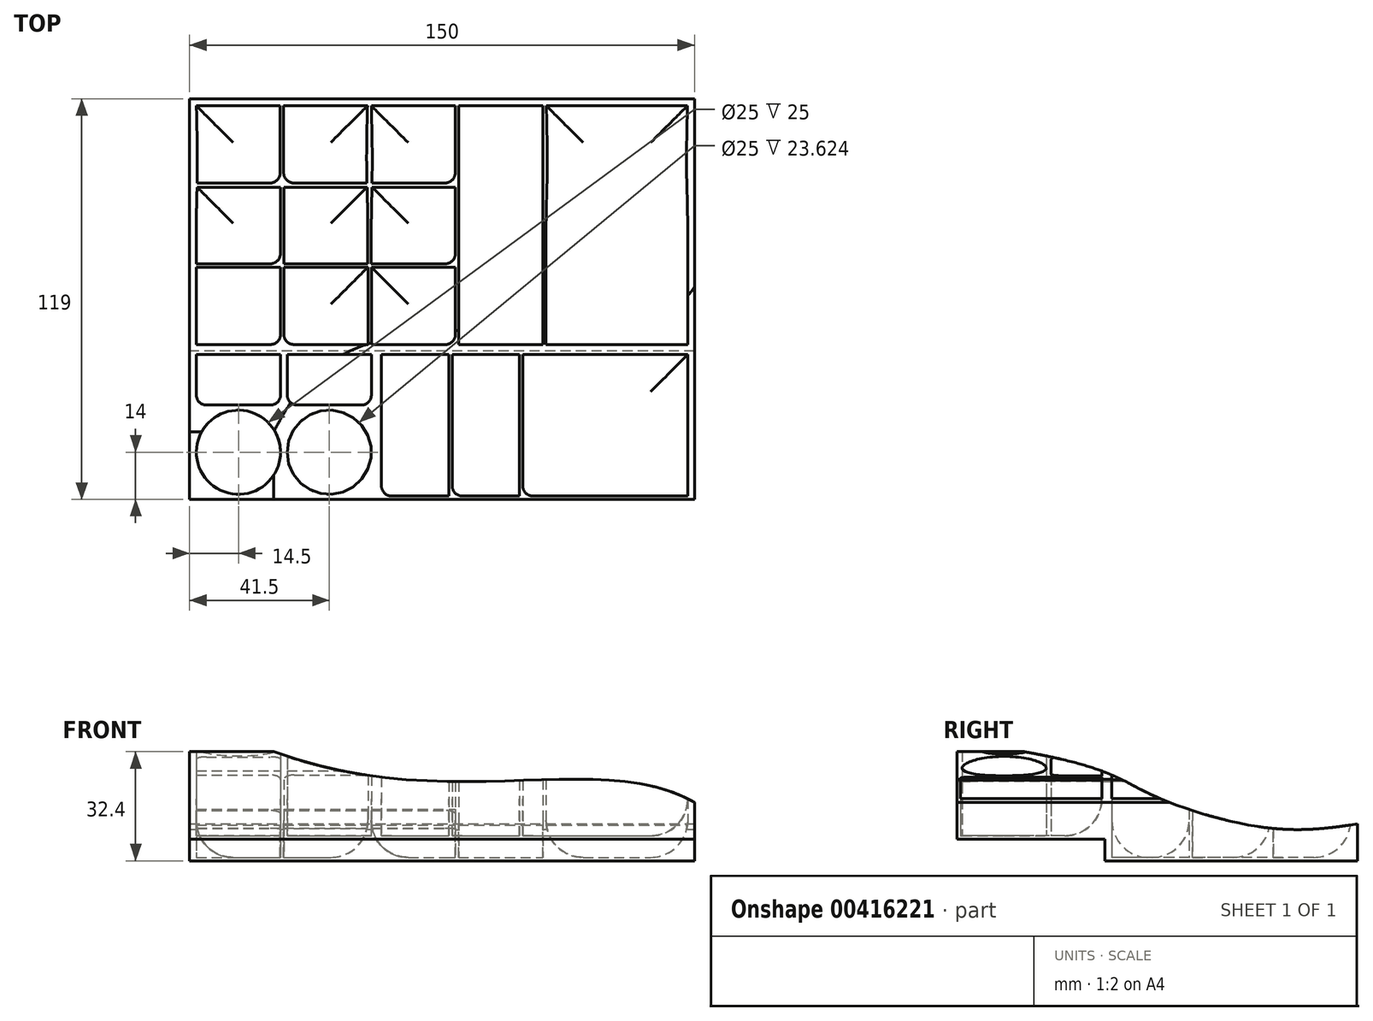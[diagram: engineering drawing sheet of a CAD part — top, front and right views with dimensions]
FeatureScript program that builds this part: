
annotation { "Feature Type Name" : "Feature", "Feature Type Description" : "" }
export const myFeature = defineFeature(function(context is Context, id is Id, definition is map)
    precondition{}
    {
        {
            var Q0;
            Q0=qCreatedBy(makeId("Right.planeOp"),FACE);
            var sketch = newSketch(context, id + "F0", { "sketchPlane" : qUnion([Q0])});
            skLineSegment(sketch, "E0", {"start": v(0, 0) * mm, "end": v(75, 0) * mm});
            skLineSegment(sketch, "E1", {"start": v(0, 0) * mm, "end": v(0, 6.4) * mm});
            skLineSegment(sketch, "E2", {"start": v(0, 6.4) * mm, "end": v(-44, 6.4) * mm});
            skLineSegment(sketch, "E3.0", {"start": v(1, 7.4) * mm, "end": v(-44, 7.4) * mm});
            skLineSegment(sketch, "E3.1", {"start": v(1, 1) * mm, "end": v(1, 7.4) * mm});
            skLineSegment(sketch, "E3.2", {"start": v(1, 1) * mm, "end": v(75, 1) * mm});
            skLineSegment(sketch, "E4", {"start": v(75, 1) * mm, "end": v(75, 0) * mm});
            skLineSegment(sketch, "E5", {"start": v(-44, 7.4) * mm, "end": v(-44, 6.4) * mm});
            skSolve(sketch);
        }
        {
            var Q0;
            Q0=makeQuery(id+"F0.imprint","IMPRINT",FACE,{"disambiguationData":[TD([[makeQuery(id+"F0.imprint","IMPRINT",EDGE,{"derivedFrom":sQuery(id+"F0.wireOp",EDGE,"E0")}),1.0]])]});
            extrude(context, id + "F1", {"entities" : qUnion([Q0]), "depth" : 150 * mm});
        }
        {
            var Q0;
            Q0=makeQuery(id+"F1.opExtrude","SWEPT_FACE",FACE,{"disambiguationData":[OSD([sQuery(id+"F0.wireOp",EDGE,"E3.0")])]});
            var sketch = newSketch(context, id + "F2", { "sketchPlane" : qUnion([Q0])});
            skCircle(sketch, "E6", {"center": v(14.5, -30) * mm, "radius": 12.5 * mm});
            skCircle(sketch, "E7", {"center": v(41.5, -30) * mm, "radius": 12.5 * mm});
            skLineSegment(sketch, "E8.bottom", {"start": v(2, -1) * mm, "end": v(27, -1) * mm});
            skLineSegment(sketch, "E8.top", {"start": v(2, -16) * mm, "end": v(27, -16) * mm});
            skLineSegment(sketch, "E8.left", {"start": v(2, -1) * mm, "end": v(2, -16) * mm});
            skLineSegment(sketch, "E8.right", {"start": v(27, -1) * mm, "end": v(27, -16) * mm});
            skLineSegment(sketch, "E9.bottom", {"start": v(29, -1) * mm, "end": v(54, -1) * mm});
            skLineSegment(sketch, "E9.top", {"start": v(29, -16) * mm, "end": v(54, -16) * mm});
            skLineSegment(sketch, "E9.left", {"start": v(29, -1) * mm, "end": v(29, -16) * mm});
            skLineSegment(sketch, "E9.right", {"start": v(54, -1) * mm, "end": v(54, -16) * mm});
            skLineSegment(sketch, "E10.bottom", {"start": v(57, -1) * mm, "end": v(77, -1) * mm});
            skLineSegment(sketch, "E10.top", {"start": v(57, -43) * mm, "end": v(77, -43) * mm});
            skLineSegment(sketch, "E10.left", {"start": v(57, -1) * mm, "end": v(57, -43) * mm});
            skLineSegment(sketch, "E10.right", {"start": v(77, -1) * mm, "end": v(77, -43) * mm});
            skLineSegment(sketch, "E11.bottom", {"start": v(78, -1) * mm, "end": v(98, -1) * mm});
            skLineSegment(sketch, "E11.top", {"start": v(78, -43) * mm, "end": v(98, -43) * mm});
            skLineSegment(sketch, "E11.left", {"start": v(78, -1) * mm, "end": v(78, -43) * mm});
            skLineSegment(sketch, "E11.right", {"start": v(98, -1) * mm, "end": v(98, -43) * mm});
            skLineSegment(sketch, "E12.bottom", {"start": v(99, -1) * mm, "end": v(148, -1) * mm});
            skLineSegment(sketch, "E12.top", {"start": v(99, -43) * mm, "end": v(148, -43) * mm});
            skLineSegment(sketch, "E12.left", {"start": v(99, -1) * mm, "end": v(99, -43) * mm});
            skLineSegment(sketch, "E12.right", {"start": v(148, -1) * mm, "end": v(148, -43) * mm});
            skLineSegment(sketch, "E13", {"start": v(27, -1) * mm, "end": v(29, -1) * mm, "construction": true});
            skLineSegment(sketch, "E14", {"start": v(54, -1) * mm, "end": v(57, -1) * mm, "construction": true});
            skLineSegment(sketch, "E15", {"start": v(77, -1) * mm, "end": v(78, -1) * mm, "construction": true});
            skLineSegment(sketch, "E16", {"start": v(98, -1) * mm, "end": v(99, -1) * mm, "construction": true});
            skLineSegment(sketch, "E17", {"start": v(14.5, -30) * mm, "end": v(14.5, -16) * mm, "construction": true});
            skLineSegment(sketch, "E18", {"start": v(41.5, -30) * mm, "end": v(41.5, -16) * mm, "construction": true});
            skLineSegment(sketch, "E19", {"start": v(0, 1) * mm, "end": v(150, 1) * mm});
            skLineSegment(sketch, "E20", {"start": v(150, 1) * mm, "end": v(150, -44) * mm});
            skLineSegment(sketch, "E21", {"start": v(150, -44) * mm, "end": v(0, -44) * mm});
            skLineSegment(sketch, "E22", {"start": v(0, -44) * mm, "end": v(0, 1) * mm});
            skSolve(sketch);
        }
        {
            var Q0;
            Q0=makeQuery(id+"F2.imprint","IMPRINT",FACE,{"disambiguationData":[TD([[makeQuery(id+"F2.imprint","IMPRINT",EDGE,{"derivedFrom":sQuery(id+"F2.wireOp",EDGE,"E6")}),-1.0]])]});
            extrude(context, id + "F3", {"entities" : qUnion([Q0]), "operationType" : NewBodyOperationType.ADD, "depth" : 25 * mm});
        }
        {
            var Q0;
            Q0=makeQuery(id+"F1.opExtrude","SWEPT_FACE",FACE,{"disambiguationData":[OSD([sQuery(id+"F0.wireOp",EDGE,"E3.2")])]});
            var sketch = newSketch(context, id + "F4", { "sketchPlane" : qUnion([Q0])});
            skLineSegment(sketch, "E23.bottom", {"start": v(1.93, 73) * mm, "end": v(26.93, 73) * mm});
            skLineSegment(sketch, "E23.top", {"start": v(1.93, 50) * mm, "end": v(26.93, 50) * mm});
            skLineSegment(sketch, "E23.left", {"start": v(1.93, 73) * mm, "end": v(1.93, 50) * mm});
            skLineSegment(sketch, "E23.right", {"start": v(26.93, 73) * mm, "end": v(26.93, 50) * mm});
            skLineSegment(sketch, "E24.0.1.0", {"start": v(26.96, 49) * mm, "end": v(26.96, 26) * mm});
            skLineSegment(sketch, "E24.0.1.1", {"start": v(1.96, 49) * mm, "end": v(26.96, 49) * mm});
            skLineSegment(sketch, "E24.0.1.2", {"start": v(1.96, 26) * mm, "end": v(26.96, 26) * mm});
            skLineSegment(sketch, "E24.0.1.3", {"start": v(1.96, 49) * mm, "end": v(1.96, 26) * mm});
            skLineSegment(sketch, "E24.0.2.0", {"start": v(27, 25) * mm, "end": v(27, 2) * mm});
            skLineSegment(sketch, "E24.0.2.1", {"start": v(2, 25) * mm, "end": v(27, 25) * mm});
            skLineSegment(sketch, "E24.0.2.2", {"start": v(2, 2) * mm, "end": v(27, 2) * mm});
            skLineSegment(sketch, "E24.0.2.3", {"start": v(2, 25) * mm, "end": v(2, 2) * mm});
            skLineSegment(sketch, "E24.1.0.0", {"start": v(52.93, 73) * mm, "end": v(52.93, 50) * mm});
            skLineSegment(sketch, "E24.1.0.1", {"start": v(27.93, 73) * mm, "end": v(52.93, 73) * mm});
            skLineSegment(sketch, "E24.1.0.2", {"start": v(27.93, 50) * mm, "end": v(52.93, 50) * mm});
            skLineSegment(sketch, "E24.1.0.3", {"start": v(27.93, 73) * mm, "end": v(27.93, 50) * mm});
            skLineSegment(sketch, "E24.1.1.0", {"start": v(52.96, 49) * mm, "end": v(52.96, 26) * mm});
            skLineSegment(sketch, "E24.1.1.1", {"start": v(27.96, 49) * mm, "end": v(52.96, 49) * mm});
            skLineSegment(sketch, "E24.1.1.2", {"start": v(27.96, 26) * mm, "end": v(52.96, 26) * mm});
            skLineSegment(sketch, "E24.1.1.3", {"start": v(27.96, 49) * mm, "end": v(27.96, 26) * mm});
            skLineSegment(sketch, "E24.1.2.0", {"start": v(53, 25) * mm, "end": v(53, 2) * mm});
            skLineSegment(sketch, "E24.1.2.1", {"start": v(28, 25) * mm, "end": v(53, 25) * mm});
            skLineSegment(sketch, "E24.1.2.2", {"start": v(28, 2) * mm, "end": v(53, 2) * mm});
            skLineSegment(sketch, "E24.1.2.3", {"start": v(28, 25) * mm, "end": v(28, 2) * mm});
            skLineSegment(sketch, "E24.2.0.0", {"start": v(78.93, 73) * mm, "end": v(78.93, 50) * mm});
            skLineSegment(sketch, "E24.2.0.1", {"start": v(53.93, 73) * mm, "end": v(78.93, 73) * mm});
            skLineSegment(sketch, "E24.2.0.2", {"start": v(53.93, 50) * mm, "end": v(78.93, 50) * mm});
            skLineSegment(sketch, "E24.2.0.3", {"start": v(53.93, 73) * mm, "end": v(53.93, 50) * mm});
            skLineSegment(sketch, "E24.2.1.0", {"start": v(78.96, 49) * mm, "end": v(78.96, 26) * mm});
            skLineSegment(sketch, "E24.2.1.1", {"start": v(53.96, 49) * mm, "end": v(78.96, 49) * mm});
            skLineSegment(sketch, "E24.2.1.2", {"start": v(53.96, 26) * mm, "end": v(78.96, 26) * mm});
            skLineSegment(sketch, "E24.2.1.3", {"start": v(53.96, 49) * mm, "end": v(53.96, 26) * mm});
            skLineSegment(sketch, "E24.2.2.0", {"start": v(79, 25) * mm, "end": v(79, 2) * mm});
            skLineSegment(sketch, "E24.2.2.1", {"start": v(54, 25) * mm, "end": v(79, 25) * mm});
            skLineSegment(sketch, "E24.2.2.2", {"start": v(54, 2) * mm, "end": v(79, 2) * mm});
            skLineSegment(sketch, "E24.2.2.3", {"start": v(54, 25) * mm, "end": v(54, 2) * mm});
            skLineSegment(sketch, "E24.direction1", {"start": v(1.93, 73) * mm, "end": v(27.93, 73) * mm, "construction": true});
            skLineSegment(sketch, "E24.direction2", {"start": v(1.93, 73) * mm, "end": v(1.96, 49) * mm, "construction": true});
            skLineSegment(sketch, "E25.bottom", {"start": v(79.93, 73) * mm, "end": v(104.93, 73) * mm});
            skLineSegment(sketch, "E25.top", {"start": v(79.93, 2) * mm, "end": v(104.93, 2) * mm});
            skLineSegment(sketch, "E25.left", {"start": v(79.93, 73) * mm, "end": v(79.93, 2) * mm});
            skLineSegment(sketch, "E25.right", {"start": v(104.93, 73) * mm, "end": v(104.93, 2) * mm});
            skLineSegment(sketch, "E26.bottom", {"start": v(105.93, 73) * mm, "end": v(148, 73) * mm});
            skLineSegment(sketch, "E26.top", {"start": v(105.93, 2) * mm, "end": v(148, 2) * mm});
            skLineSegment(sketch, "E26.left", {"start": v(105.93, 73) * mm, "end": v(105.93, 2) * mm});
            skLineSegment(sketch, "E26.right", {"start": v(148, 73) * mm, "end": v(148, 2) * mm});
            skLineSegment(sketch, "E27", {"start": v(104.93, 73) * mm, "end": v(105.93, 73) * mm, "construction": true});
            skLineSegment(sketch, "E28", {"start": v(78.93, 73) * mm, "end": v(79.93, 73) * mm, "construction": true});
            skLineSegment(sketch, "E29", {"start": v(79, 2) * mm, "end": v(79.93, 2) * mm, "construction": true});
            skLineSegment(sketch, "E30", {"start": v(104.93, 2) * mm, "end": v(105.93, 2) * mm, "construction": true});
            skLineSegment(sketch, "E31", {"start": v(0, 1) * mm, "end": v(0, 75) * mm});
            skLineSegment(sketch, "E32", {"start": v(0, 75) * mm, "end": v(150, 75) * mm});
            skLineSegment(sketch, "E33", {"start": v(150, 75) * mm, "end": v(150, 1) * mm});
            skLineSegment(sketch, "E34", {"start": v(150, 1) * mm, "end": v(0, 1) * mm});
            skSolve(sketch);
        }
        {
            var Q0;
            Q0=makeQuery(id+"F4.imprint","IMPRINT",FACE,{"disambiguationData":[TD([[makeQuery(id+"F4.imprint","IMPRINT",EDGE,{"derivedFrom":sQuery(id+"F4.wireOp",EDGE,"E23.bottom")}),1.0]])]});
            var Q1;
            Q1=makeQuery(id+"F3.opExtrude","CAP_FACE",FACE,{"disambiguationData":[OSD([sQuery(id+"F2.wireOp",EDGE,"E6"),sQuery(id+"F2.wireOp",EDGE,"E7"),sQuery(id+"F2.wireOp",EDGE,"E8.bottom"),sQuery(id+"F2.wireOp",EDGE,"E8.top"),sQuery(id+"F2.wireOp",EDGE,"E8.left"),sQuery(id+"F2.wireOp",EDGE,"E8.right"),sQuery(id+"F2.wireOp",EDGE,"E9.bottom"),sQuery(id+"F2.wireOp",EDGE,"E9.top"),sQuery(id+"F2.wireOp",EDGE,"E9.left"),sQuery(id+"F2.wireOp",EDGE,"E9.right"),sQuery(id+"F2.wireOp",EDGE,"E10.bottom"),sQuery(id+"F2.wireOp",EDGE,"E10.top"),sQuery(id+"F2.wireOp",EDGE,"E10.left"),sQuery(id+"F2.wireOp",EDGE,"E10.right"),sQuery(id+"F2.wireOp",EDGE,"E11.bottom"),sQuery(id+"F2.wireOp",EDGE,"E11.top"),sQuery(id+"F2.wireOp",EDGE,"E11.left"),sQuery(id+"F2.wireOp",EDGE,"E11.right"),sQuery(id+"F2.wireOp",EDGE,"E12.bottom"),sQuery(id+"F2.wireOp",EDGE,"E12.top"),sQuery(id+"F2.wireOp",EDGE,"E12.left"),sQuery(id+"F2.wireOp",EDGE,"E12.right"),sQuery(id+"F2.wireOp",EDGE,"E19"),sQuery(id+"F2.wireOp",EDGE,"E20"),sQuery(id+"F2.wireOp",EDGE,"E21"),sQuery(id+"F2.wireOp",EDGE,"E22")])],"isStart":false});
            extrude(context, id + "F5", {"entities" : qUnion([Q0]), "operationType" : NewBodyOperationType.ADD, "endBound" : BoundingType.UP_TO_SURFACE, "endBoundEntityFace" : qUnion([Q1]), "depth" : 25 * mm});
        }
        {
            var Q0;
            Q0=makeQuery(id+"F3.opExtrude","CAP_EDGE",EDGE,{"disambiguationData":[OSD([sQuery(id+"F2.wireOp",EDGE,"E7")])],"isStart":true});
            var Q1;
            Q1=makeQuery(id+"F3.opExtrude","CAP_EDGE",EDGE,{"disambiguationData":[OSD([sQuery(id+"F2.wireOp",EDGE,"E9.bottom")])],"isStart":true});
            var Q2;
            Q2=makeQuery(id+"F3.opExtrude","CAP_EDGE",EDGE,{"disambiguationData":[OSD([sQuery(id+"F2.wireOp",EDGE,"E10.bottom")])],"isStart":true});
            var Q3;
            Q3=makeQuery(id+"F3.opExtrude","CAP_EDGE",EDGE,{"disambiguationData":[OSD([sQuery(id+"F2.wireOp",EDGE,"E11.bottom")])],"isStart":true});
            var Q4;
            Q4=makeQuery(id+"F3.opExtrude","CAP_EDGE",EDGE,{"disambiguationData":[OSD([sQuery(id+"F2.wireOp",EDGE,"E12.bottom")])],"isStart":true});
            var Q5;
            Q5=makeQuery(id+"F5.opExtrude","CAP_EDGE",EDGE,{"disambiguationData":[OSD([sQuery(id+"F4.wireOp",EDGE,"E24.0.2.3")])],"isStart":true});
            var Q6;
            Q6=makeQuery(id+"F5.opExtrude","CAP_EDGE",EDGE,{"disambiguationData":[OSD([sQuery(id+"F4.wireOp",EDGE,"E24.0.1.3")])],"isStart":true});
            var Q7;
            Q7=makeQuery(id+"F5.opExtrude","CAP_EDGE",EDGE,{"disambiguationData":[OSD([sQuery(id+"F4.wireOp",EDGE,"E23.left")])],"isStart":true});
            var Q8;
            Q8=makeQuery(id+"F5.opExtrude","CAP_EDGE",EDGE,{"disambiguationData":[OSD([sQuery(id+"F4.wireOp",EDGE,"E24.1.2.1")])],"isStart":true});
            var Q9;
            Q9=makeQuery(id+"F5.opExtrude","CAP_EDGE",EDGE,{"disambiguationData":[OSD([sQuery(id+"F4.wireOp",EDGE,"E24.1.1.1")])],"isStart":true});
            var Q10;
            Q10=makeQuery(id+"F5.opExtrude","CAP_EDGE",EDGE,{"disambiguationData":[OSD([sQuery(id+"F4.wireOp",EDGE,"E24.1.0.1")])],"isStart":true});
            var Q11;
            Q11=makeQuery(id+"F5.opExtrude","CAP_EDGE",EDGE,{"disambiguationData":[OSD([sQuery(id+"F4.wireOp",EDGE,"E24.2.0.1")])],"isStart":true});
            var Q12;
            Q12=makeQuery(id+"F5.opExtrude","CAP_EDGE",EDGE,{"disambiguationData":[OSD([sQuery(id+"F4.wireOp",EDGE,"E24.2.1.1")])],"isStart":true});
            var Q13;
            Q13=makeQuery(id+"F5.opExtrude","CAP_EDGE",EDGE,{"disambiguationData":[OSD([sQuery(id+"F4.wireOp",EDGE,"E24.2.2.1")])],"isStart":true});
            var Q14;
            Q14=makeQuery(id+"F5.opExtrude","CAP_EDGE",EDGE,{"disambiguationData":[OSD([sQuery(id+"F4.wireOp",EDGE,"E25.top")])],"isStart":true});
            var Q15;
            Q15=makeQuery(id+"F5.opExtrude","CAP_EDGE",EDGE,{"disambiguationData":[OSD([sQuery(id+"F4.wireOp",EDGE,"E25.bottom")])],"isStart":true});
            var Q16;
            Q16=makeQuery(id+"F5.opExtrude","CAP_EDGE",EDGE,{"disambiguationData":[OSD([sQuery(id+"F4.wireOp",EDGE,"E26.left")])],"isStart":true});
            var Q17;
            Q17=makeQuery(id+"F5.opExtrude","CAP_EDGE",EDGE,{"disambiguationData":[OSD([sQuery(id+"F4.wireOp",EDGE,"E26.bottom")])],"isStart":true});
            var Q18;
            Q18=makeQuery(id+"F5.opExtrude","CAP_EDGE",EDGE,{"disambiguationData":[OSD([sQuery(id+"F4.wireOp",EDGE,"E26.right")])],"isStart":true});
            var Q19;
            Q19=makeQuery(id+"F3.opExtrude","CAP_EDGE",EDGE,{"disambiguationData":[OSD([sQuery(id+"F2.wireOp",EDGE,"E8.bottom")])],"isStart":true});
            var Q20;
            Q20=makeQuery(id+"F5.opExtrude","CAP_EDGE",EDGE,{"disambiguationData":[OSD([sQuery(id+"F4.wireOp",EDGE,"E24.1.2.0")])],"isStart":true});
            var Q21;
            Q21=makeQuery(id+"F5.opExtrude","CAP_EDGE",EDGE,{"disambiguationData":[OSD([sQuery(id+"F4.wireOp",EDGE,"E24.1.1.0")])],"isStart":true});
            var Q22;
            Q22=makeQuery(id+"F5.opExtrude","CAP_EDGE",EDGE,{"disambiguationData":[OSD([sQuery(id+"F4.wireOp",EDGE,"E24.1.0.0")])],"isStart":true});
            var Q23;
            Q23=makeQuery(id+"F5.opExtrude","CAP_EDGE",EDGE,{"disambiguationData":[OSD([sQuery(id+"F4.wireOp",EDGE,"E24.2.0.3")])],"isStart":true});
            var Q24;
            Q24=makeQuery(id+"F5.opExtrude","CAP_EDGE",EDGE,{"disambiguationData":[OSD([sQuery(id+"F4.wireOp",EDGE,"E24.2.1.3")])],"isStart":true});
            var Q25;
            Q25=makeQuery(id+"F5.opExtrude","CAP_EDGE",EDGE,{"disambiguationData":[OSD([sQuery(id+"F4.wireOp",EDGE,"E24.2.2.3")])],"isStart":true});
            var Q26;
            Q26=makeQuery(id+"F5.opExtrude","CAP_EDGE",EDGE,{"disambiguationData":[OSD([sQuery(id+"F4.wireOp",EDGE,"E23.bottom")])],"isStart":true});
            var Q27;
            Q27=makeQuery(id+"F5.opExtrude","CAP_EDGE",EDGE,{"disambiguationData":[OSD([sQuery(id+"F4.wireOp",EDGE,"E24.0.1.1")])],"isStart":true});
            var Q28;
            Q28=makeQuery(id+"F5.opExtrude","CAP_EDGE",EDGE,{"disambiguationData":[OSD([sQuery(id+"F4.wireOp",EDGE,"E24.0.2.1")])],"isStart":true});
            var Q29;
            Q29=makeQuery(id+"F3.opExtrude","CAP_EDGE",EDGE,{"disambiguationData":[OSD([sQuery(id+"F2.wireOp",EDGE,"E12.right")])],"isStart":true});
            fillet(context, id + "F6", {"entities" : qUnion([Q0, Q1, Q2, Q3, Q4, Q5, Q6, Q7, Q8, Q9, Q10, Q11, Q12, Q13, Q14, Q15, Q16, Q17, Q18, Q19, Q20, Q21, Q22, Q23, Q24, Q25, Q26, Q27, Q28, Q29]), "radius" : 11 * mm, "tangentPropagation" : true, "allowEdgeOverflow" : false});
        }
        {
            var Q0;
            Q0=makeQuery(id+"F3.boolean.opBoolean","MERGE",FACE,{"derivedFrom":[makeQuery(id+"F1.opExtrude","SWEPT_FACE",FACE,{"disambiguationData":[OSD([sQuery(id+"F0.wireOp",EDGE,"E5")])]}),makeQuery(id+"F3.opExtrude","SWEPT_FACE",FACE,{"disambiguationData":[OSD([sQuery(id+"F2.wireOp",EDGE,"E21")])]})]});
            var sketch = newSketch(context, id + "F7", { "sketchPlane" : qUnion([Q0])});
            skFitSpline(sketch, "E35", {"points": [v(25, 32.4) * mm, v(105.5, 24.11) * mm, v(150, 17.4) * mm], "startDerivative": vector(159.73, -57.6) * mm, "endDerivative": vector(83.87, -47.9) * mm});
            skLineSegment(sketch, "E36", {"start": v(25, 32.4) * mm, "end": v(150, 32.4) * mm});
            skLineSegment(sketch, "E37", {"start": v(150, 32.4) * mm, "end": v(150, 17.4) * mm});
            skSolve(sketch);
        }
        {
            var Q0;
            Q0=makeQuery(id+"F5.boolean.opBoolean","MERGE",FACE,{"derivedFrom":[makeQuery(id+"F3.boolean.opBoolean","MERGE",FACE,{"derivedFrom":[makeQuery(id+"F1.opExtrude","CAP_FACE",FACE,{"disambiguationData":[OSD([sQuery(id+"F0.wireOp",EDGE,"E0"),sQuery(id+"F0.wireOp",EDGE,"E1"),sQuery(id+"F0.wireOp",EDGE,"E2"),sQuery(id+"F0.wireOp",EDGE,"E3.0"),sQuery(id+"F0.wireOp",EDGE,"E3.1"),sQuery(id+"F0.wireOp",EDGE,"E3.2"),sQuery(id+"F0.wireOp",EDGE,"E4"),sQuery(id+"F0.wireOp",EDGE,"E5")])],"isStart":false}),makeQuery(id+"F3.opExtrude","SWEPT_FACE",FACE,{"disambiguationData":[OSD([sQuery(id+"F2.wireOp",EDGE,"E20")])]})]}),makeQuery(id+"F5.opExtrude","SWEPT_FACE",FACE,{"disambiguationData":[OSD([sQuery(id+"F4.wireOp",EDGE,"E33")])]})]});
            var sketch = newSketch(context, id + "F8", { "sketchPlane" : qUnion([Q0])});
            skFitSpline(sketch, "E38", {"points": [v(-24, 32.4) * mm, v(13.42, 19.8) * mm, v(48.08, 9.82) * mm, v(75, 11) * mm], "startDerivative": vector(209.63, -37.34) * mm, "endDerivative": vector(82.09, 13.74) * mm});
            skLineSegment(sketch, "E39", {"start": v(75, 11) * mm, "end": v(75, 32.4) * mm});
            skLineSegment(sketch, "E40", {"start": v(75, 32.4) * mm, "end": v(-24, 32.4) * mm});
            skSolve(sketch);
        }
        {
            var Q0;
            Q0=makeQuery(id+"F7.imprint","IMPRINT",FACE,{"disambiguationData":[TD([[makeQuery(id+"F7.imprint","IMPRINT",EDGE,{"derivedFrom":sQuery(id+"F7.wireOp",EDGE,"E35")}),1.0]])]});
            extrude(context, id + "F9", {"entities" : qUnion([Q0]), "operationType" : NewBodyOperationType.REMOVE, "endBound" : BoundingType.THROUGH_ALL, "oppositeDirection" : true, "depth" : 25 * mm});
        }
        {
            var Q0;
            Q0=makeQuery(id+"F8.imprint","IMPRINT",FACE,{"disambiguationData":[TD([[makeQuery(id+"F8.imprint","IMPRINT",EDGE,{"derivedFrom":sQuery(id+"F8.wireOp",EDGE,"E38")}),1.0]])]});
            extrude(context, id + "F10", {"entities" : qUnion([Q0]), "operationType" : NewBodyOperationType.REMOVE, "endBound" : BoundingType.THROUGH_ALL, "oppositeDirection" : true, "depth" : 25 * mm});
        }
        {
            var Q0;
            Q0=makeQuery(id+"F3.opExtrude","SWEPT_EDGE",EDGE,{"disambiguationData":[OSD([sQuery(id+"F2.wireOp",EDGE,"E12.top"),sQuery(id+"F2.wireOp",EDGE,"E12.left")])]});
            var Q1;
            Q1=makeQuery(id+"F3.opExtrude","SWEPT_EDGE",EDGE,{"disambiguationData":[OSD([sQuery(id+"F2.wireOp",EDGE,"E11.top"),sQuery(id+"F2.wireOp",EDGE,"E11.left")])]});
            var Q2;
            Q2=makeQuery(id+"F3.opExtrude","SWEPT_EDGE",EDGE,{"disambiguationData":[OSD([sQuery(id+"F2.wireOp",EDGE,"E10.top"),sQuery(id+"F2.wireOp",EDGE,"E10.left")])]});
            var Q3;
            Q3=makeQuery(id+"F3.opExtrude","SWEPT_EDGE",EDGE,{"disambiguationData":[OSD([sQuery(id+"F2.wireOp",EDGE,"E9.top"),sQuery(id+"F2.wireOp",EDGE,"E9.left")])]});
            var Q4;
            Q4=makeQuery(id+"F3.opExtrude","SWEPT_EDGE",EDGE,{"disambiguationData":[OSD([sQuery(id+"F2.wireOp",EDGE,"E8.top"),sQuery(id+"F2.wireOp",EDGE,"E8.left")])]});
            var Q5;
            Q5=makeQuery(id+"F5.opExtrude","SWEPT_EDGE",EDGE,{"disambiguationData":[OSD([sQuery(id+"F4.wireOp",EDGE,"E24.1.2.2"),sQuery(id+"F4.wireOp",EDGE,"E24.1.2.3")])]});
            var Q6;
            Q6=makeQuery(id+"F5.opExtrude","SWEPT_EDGE",EDGE,{"disambiguationData":[OSD([sQuery(id+"F4.wireOp",EDGE,"E24.0.2.0"),sQuery(id+"F4.wireOp",EDGE,"E24.0.2.2")])]});
            var Q7;
            Q7=makeQuery(id+"F5.opExtrude","SWEPT_EDGE",EDGE,{"disambiguationData":[OSD([sQuery(id+"F4.wireOp",EDGE,"E24.2.2.0"),sQuery(id+"F4.wireOp",EDGE,"E24.2.2.2")])]});
            var Q8;
            Q8=makeQuery(id+"F5.opExtrude","SWEPT_EDGE",EDGE,{"disambiguationData":[OSD([sQuery(id+"F4.wireOp",EDGE,"E24.0.1.0"),sQuery(id+"F4.wireOp",EDGE,"E24.0.1.2")])]});
            var Q9;
            Q9=makeQuery(id+"F5.opExtrude","SWEPT_EDGE",EDGE,{"disambiguationData":[OSD([sQuery(id+"F4.wireOp",EDGE,"E23.top"),sQuery(id+"F4.wireOp",EDGE,"E23.right")])]});
            var Q10;
            Q10=makeQuery(id+"F5.opExtrude","SWEPT_EDGE",EDGE,{"disambiguationData":[OSD([sQuery(id+"F4.wireOp",EDGE,"E24.1.0.2"),sQuery(id+"F4.wireOp",EDGE,"E24.1.0.3")])]});
            var Q11;
            Q11=makeQuery(id+"F5.opExtrude","SWEPT_EDGE",EDGE,{"disambiguationData":[OSD([sQuery(id+"F4.wireOp",EDGE,"E24.2.0.0"),sQuery(id+"F4.wireOp",EDGE,"E24.2.0.2")])]});
            var Q12;
            Q12=makeQuery(id+"F5.opExtrude","SWEPT_EDGE",EDGE,{"disambiguationData":[OSD([sQuery(id+"F4.wireOp",EDGE,"E24.2.1.0"),sQuery(id+"F4.wireOp",EDGE,"E24.2.1.2")])]});
            var Q13;
            Q13=makeQuery(id+"F3.opExtrude","SWEPT_EDGE",EDGE,{"disambiguationData":[OSD([sQuery(id+"F2.wireOp",EDGE,"E9.top"),sQuery(id+"F2.wireOp",EDGE,"E9.right")])]});
            var Q14;
            Q14=makeQuery(id+"F3.opExtrude","SWEPT_EDGE",EDGE,{"disambiguationData":[OSD([sQuery(id+"F2.wireOp",EDGE,"E8.top"),sQuery(id+"F2.wireOp",EDGE,"E8.right")])]});
            fillet(context, id + "F11", {"entities" : qUnion([Q0, Q1, Q2, Q3, Q4, Q5, Q6, Q7, Q8, Q9, Q10, Q11, Q12, Q13, Q14]), "radius" : 3 * mm, "tangentPropagation" : true, "allowEdgeOverflow" : false});
        }
    });
